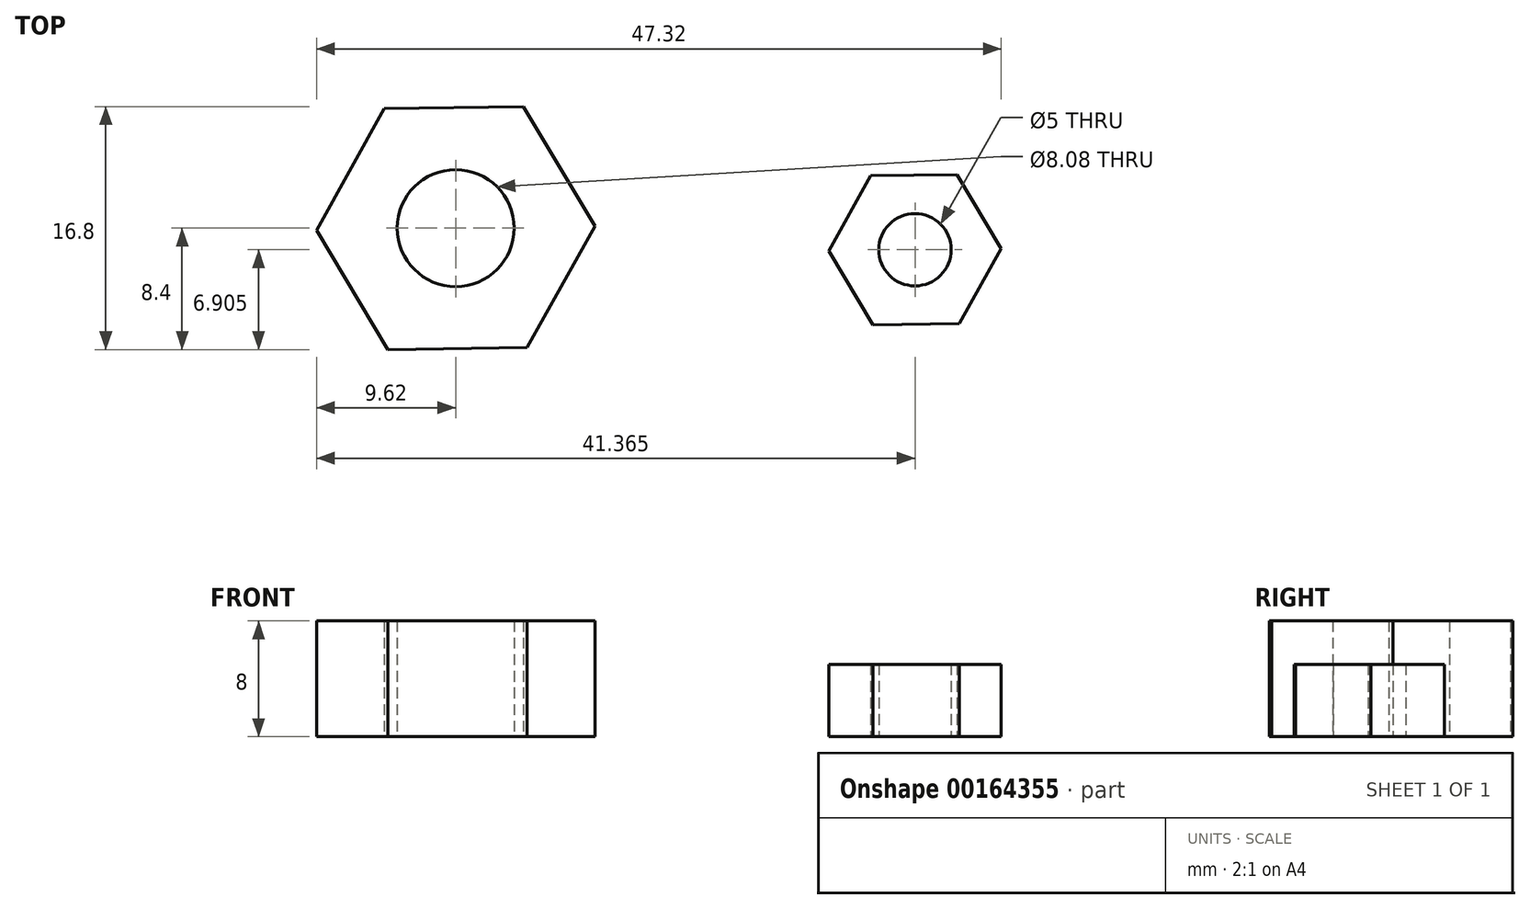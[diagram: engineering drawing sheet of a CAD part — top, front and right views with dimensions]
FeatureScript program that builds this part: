
annotation { "Feature Type Name" : "Feature", "Feature Type Description" : "" }
export const myFeature = defineFeature(function(context is Context, id is Id, definition is map)
    precondition{}
    {
        {
            var Q0;
            Q0=qCreatedBy(makeId("Top.planeOp"),FACE);
            var sketch = newSketch(context, id + "F0", { "sketchPlane" : qUnion([Q0])});
            skCircle(sketch, "E0.cCircle", {"center": v(0, 0) * mm, "radius": 8.33 * mm, "construction": true});
            skLineSegment(sketch, "E0.0", {"start": v(4.69, 8.4) * mm, "end": v(9.62, 0.14) * mm});
            skLineSegment(sketch, "E0.1", {"start": v(9.62, 0.14) * mm, "end": v(4.93, -8.26) * mm});
            skLineSegment(sketch, "E0.2", {"start": v(4.93, -8.26) * mm, "end": v(-4.69, -8.4) * mm});
            skLineSegment(sketch, "E0.3", {"start": v(-4.69, -8.4) * mm, "end": v(-9.62, -0.14) * mm});
            skLineSegment(sketch, "E0.4", {"start": v(-9.62, -0.14) * mm, "end": v(-4.93, 8.26) * mm});
            skLineSegment(sketch, "E0.5", {"start": v(-4.93, 8.26) * mm, "end": v(4.69, 8.4) * mm});
            skPoint(sketch, "E0.0.midPoint", {"position": v(7.15, 4.27) * mm});
            skCircle(sketch, "E1", {"center": v(0, 0) * mm, "radius": 4.04 * mm});
            skSolve(sketch);
        }
        {
            var Q0;
            Q0=qSketchRegion(id+"F0",true);
            extrude(context, id + "F1", {"entities" : qUnion([Q0]), "depth" : 8 * mm});
        }
        {
            var Q0;
            Q0=qCreatedBy(makeId("Top.planeOp"),FACE);
            var sketch = newSketch(context, id + "F2", { "sketchPlane" : qUnion([Q0])});
            skCircle(sketch, "E2.cCircle", {"center": v(31.75, -1.5) * mm, "radius": 5.16 * mm, "construction": true});
            skLineSegment(sketch, "E2.0", {"start": v(34.64, 3.7) * mm, "end": v(37.7, -1.4) * mm});
            skLineSegment(sketch, "E2.1", {"start": v(37.7, -1.4) * mm, "end": v(34.8, -6.6) * mm});
            skLineSegment(sketch, "E2.2", {"start": v(34.8, -6.6) * mm, "end": v(28.85, -6.7) * mm});
            skLineSegment(sketch, "E2.3", {"start": v(28.85, -6.7) * mm, "end": v(25.8, -1.58) * mm});
            skLineSegment(sketch, "E2.4", {"start": v(25.8, -1.58) * mm, "end": v(28.7, 3.62) * mm});
            skLineSegment(sketch, "E2.5", {"start": v(28.7, 3.62) * mm, "end": v(34.64, 3.7) * mm});
            skPoint(sketch, "E2.0.midPoint", {"position": v(36.17, 1.15) * mm});
            skCircle(sketch, "E3", {"center": v(31.75, -1.5) * mm, "radius": 2.5 * mm});
            skSolve(sketch);
        }
        {
            var Q0;
            Q0 = qSketchRegion(id + "F2", true);
            extrude(context, id + "F3", {"entities" : qUnion([Q0]), "depth" : 5 * mm});
        }
    });
